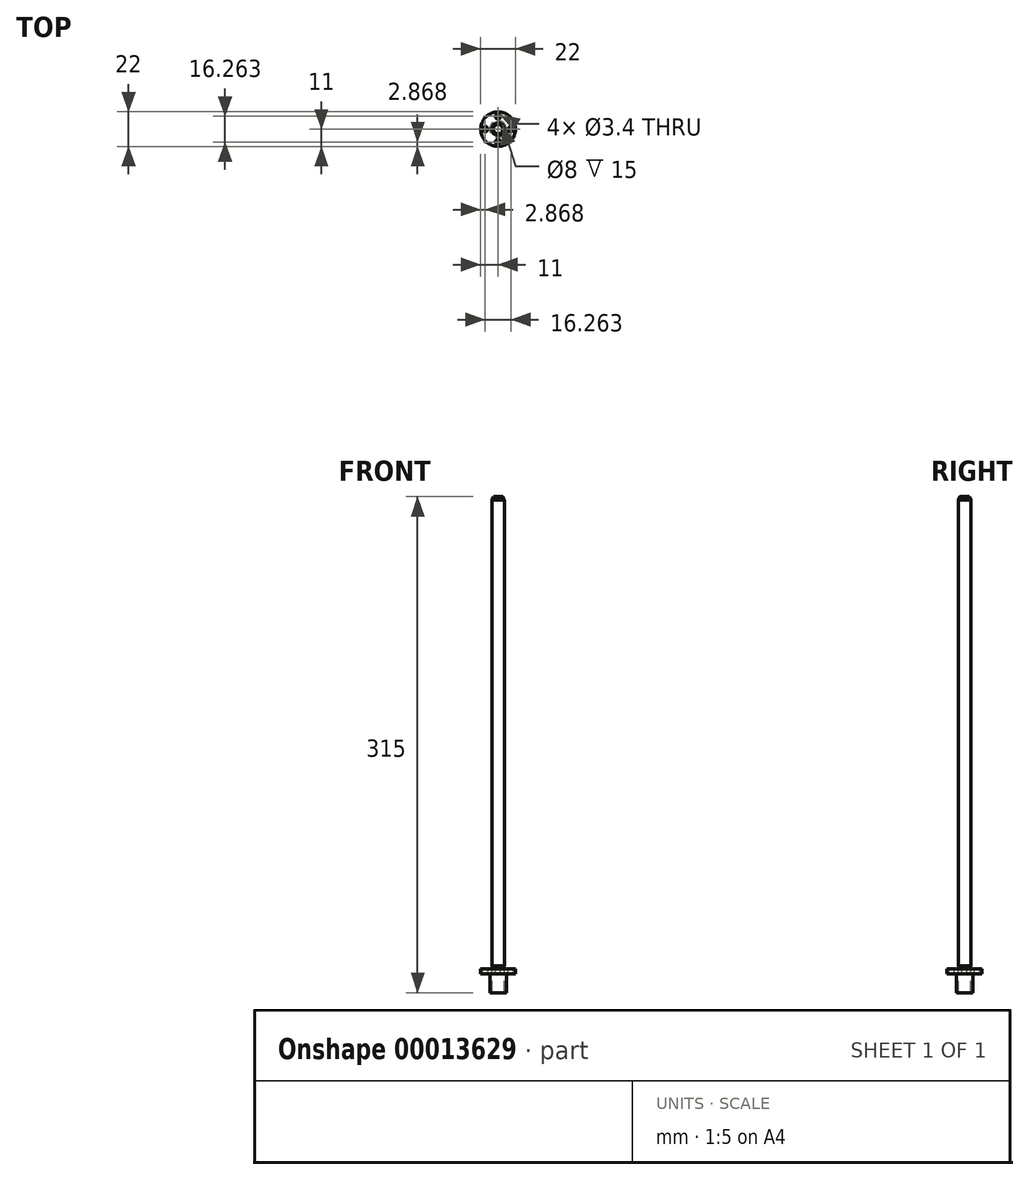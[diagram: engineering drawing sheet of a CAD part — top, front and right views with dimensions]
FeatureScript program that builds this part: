
annotation { "Feature Type Name" : "Feature", "Feature Type Description" : "" }
export const myFeature = defineFeature(function(context is Context, id is Id, definition is map)
    precondition{}
    {
        {
            var Q0;
            Q0=qCreatedBy(makeId("Top.planeOp"),FACE);
            var sketch = newSketch(context, id + "F0", { "sketchPlane" : qUnion([Q0])});
            skCircle(sketch, "E0", {"center": v(0, 0) * mm, "radius": 4 * mm});
            skSolve(sketch);
        }
        {
            var Q0;
            Q0=makeQuery(id+"F0.imprint","IMPRINT",FACE,{"disambiguationData":[TD([[makeQuery(id+"F0.imprint","IMPRINT",EDGE,{"derivedFrom":sQuery(id+"F0.wireOp",EDGE,"E0")}),1.0]])]});
            extrude(context, id + "F1", {"entities" : qUnion([Q0]), "depth" : 300 * mm});
        }
        {
            var Q0;
            Q0=makeQuery(id+"F1.opExtrude","CAP_EDGE",EDGE,{"disambiguationData":[OSD([sQuery(id+"F0.wireOp",EDGE,"E0")])],"isStart":true});
            var Q1;
            Q1=makeQuery(id+"F1.opExtrude","CAP_EDGE",EDGE,{"disambiguationData":[OSD([sQuery(id+"F0.wireOp",EDGE,"E0")])],"isStart":false});
            chamfer(context, id + "F2", {"entities" : qUnion([Q0, Q1]), "chamferType" : ChamferType.TWO_OFFSETS, "width1" : 2 * mm, "oppositeDirection" : false, "width2" : 1 * mm, "tangentPropagation" : true});
        }
        {
            var Q0;
            Q0=qCreatedBy(makeId("Top.planeOp"),FACE);
            var sketch = newSketch(context, id + "F3", { "sketchPlane" : qUnion([Q0])});
            skCircle(sketch, "E1", {"center": v(0, 0) * mm, "radius": 11 * mm});
            skCircle(sketch, "E2", {"center": v(0, 0) * mm, "radius": 5.25 * mm});
            skCircle(sketch, "E3", {"center": v(0, 0) * mm, "radius": 8.13 * mm, "construction": true});
            skCircle(sketch, "E4", {"center": v(0, 8.13) * mm, "radius": 1.7 * mm});
            skCircle(sketch, "E5.1.0", {"center": v(-8.13, 0) * mm, "radius": 1.7 * mm});
            skCircle(sketch, "E5.2.0", {"center": v(0, -8.13) * mm, "radius": 1.7 * mm});
            skCircle(sketch, "E5.3.0", {"center": v(8.13, 0) * mm, "radius": 1.7 * mm});
            skCircle(sketch, "E6", {"center": v(0, 0) * mm, "radius": 4 * mm});
            skSolve(sketch);
        }
        {
            var Q0;
            Q0=makeQuery(id+"F3.imprint","IMPRINT",FACE,{"disambiguationData":[TD([[makeQuery(id+"F3.imprint","IMPRINT",EDGE,{"derivedFrom":sQuery(id+"F3.wireOp",EDGE,"E1")}),1.0]])]});
            var Q1;
            Q1=makeQuery(id+"F3.imprint","IMPRINT",FACE,{"disambiguationData":[TD([[makeQuery(id+"F3.imprint","IMPRINT",EDGE,{"derivedFrom":sQuery(id+"F3.wireOp",EDGE,"E2")}),1.0]])]});
            extrude(context, id + "F4", {"entities" : qUnion([Q0, Q1]), "oppositeDirection" : true, "depth" : 3 * mm});
        }
        {
            var Q0;
            Q0=makeQuery(id+"F3.imprint","IMPRINT",FACE,{"disambiguationData":[TD([[makeQuery(id+"F3.imprint","IMPRINT",EDGE,{"derivedFrom":sQuery(id+"F3.wireOp",EDGE,"E2")}),1.0]])]});
            extrude(context, id + "F5", {"entities" : qUnion([Q0]), "operationType" : NewBodyOperationType.ADD, "oppositeDirection" : true, "depth" : 15 * mm});
        }
    });
